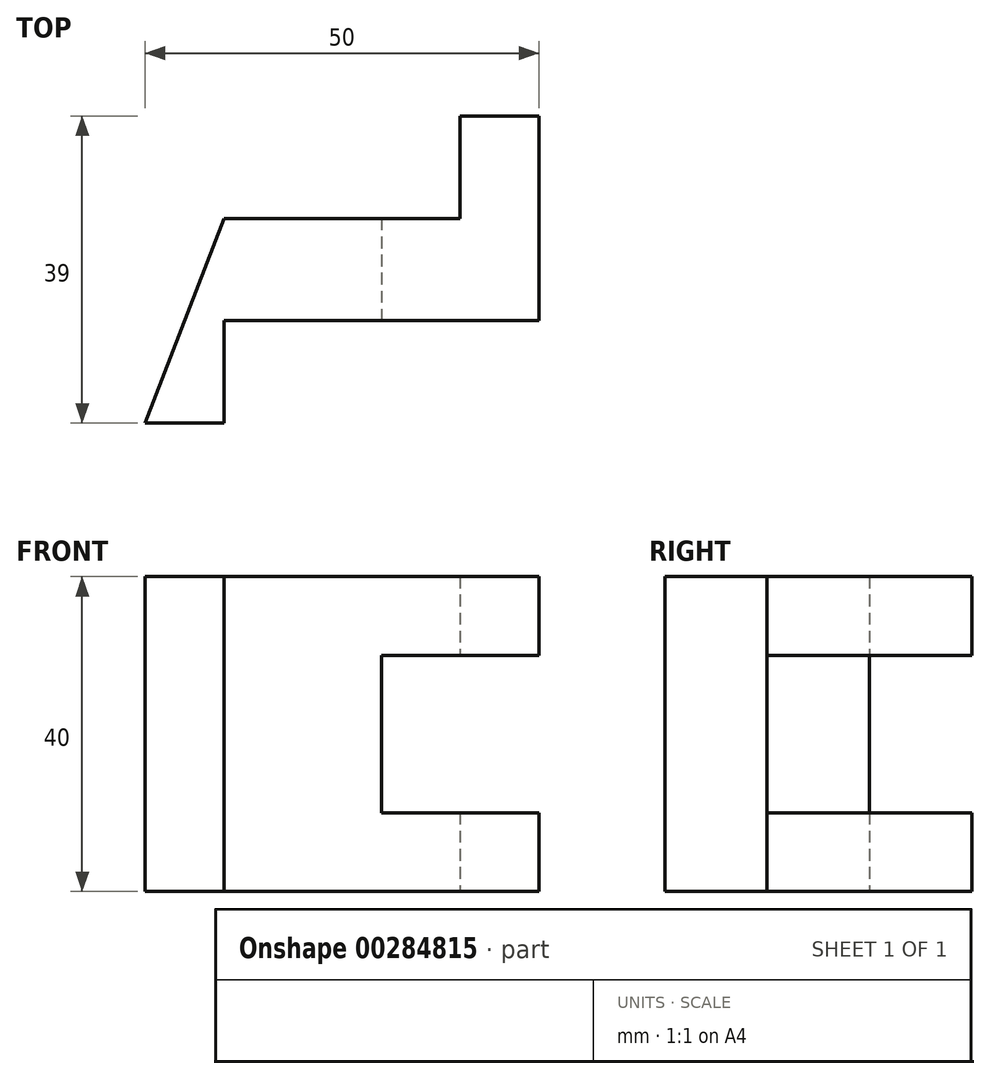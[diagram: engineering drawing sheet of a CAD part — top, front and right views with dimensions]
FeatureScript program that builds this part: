
annotation { "Feature Type Name" : "Feature", "Feature Type Description" : "" }
export const myFeature = defineFeature(function(context is Context, id is Id, definition is map)
    precondition{}
    {
        {
            var Q0;
            Q0=qCreatedBy(makeId("Top.planeOp"),FACE);
            var sketch = newSketch(context, id + "F0", { "sketchPlane" : qUnion([Q0])});
            skLineSegment(sketch, "E0.bottom", {"start": v(0, 0) * mm, "end": v(50, 0) * mm});
            skLineSegment(sketch, "E0.top", {"start": v(0, 39) * mm, "end": v(50, 39) * mm});
            skLineSegment(sketch, "E0.left", {"start": v(0, 0) * mm, "end": v(0, 39) * mm});
            skLineSegment(sketch, "E0.right", {"start": v(50, 0) * mm, "end": v(50, 39) * mm});
            skLineSegment(sketch, "E1", {"start": v(10, 0) * mm, "end": v(10, 13) * mm});
            skLineSegment(sketch, "E2", {"start": v(10, 13) * mm, "end": v(50, 13) * mm});
            skLineSegment(sketch, "E3", {"start": v(40, 39) * mm, "end": v(40, 26) * mm});
            skLineSegment(sketch, "E4", {"start": v(40, 26) * mm, "end": v(0, 26) * mm});
            skSolve(sketch);
        }
        {
            var Q0;
            {var subQ9=sQuery(id+"F0.wireOp",EDGE,"E1");Q0=makeQuery(id+"F0.imprint","IMPRINT",FACE,{"disambiguationData":[TD([[makeQuery(id+"F0.imprint","IMPRINT",EDGE,{"derivedFrom":subQ9}),1.0]])]});}
            extrude(context, id + "F1", {"entities" : qUnion([Q0]), "depth" : 40 * mm, "symmetric" : true});
        }
        {
            var Q0;
            Q0=makeQuery(id+"F1.opExtrude","SWEPT_FACE",FACE,{"disambiguationData":[OSD([sQuery(id+"F0.wireOp",EDGE,"E2")])]});
            var sketch = newSketch(context, id + "F2", { "sketchPlane" : qUnion([Q0])});
            skLineSegment(sketch, "E5.bottom", {"start": v(50, 10) * mm, "end": v(30, 10) * mm});
            skLineSegment(sketch, "E5.top", {"start": v(50, -10) * mm, "end": v(30, -10) * mm});
            skLineSegment(sketch, "E5.left", {"start": v(50, 10) * mm, "end": v(50, -10) * mm});
            skLineSegment(sketch, "E5.right", {"start": v(30, 10) * mm, "end": v(30, -10) * mm});
            skSolve(sketch);
        }
        {
            var Q0;
            Q0=qSketchRegion(id+"F2",true);
            extrude(context, id + "F3", {"entities" : qUnion([Q0]), "operationType" : NewBodyOperationType.REMOVE, "endBound" : BoundingType.THROUGH_ALL, "oppositeDirection" : true, "depth" : 25 * mm});
        }
        {
            var Q0;
            Q0=makeQuery(id+"F1.opExtrude","CAP_FACE",FACE,{"disambiguationData":[OSD([sQuery(id+"F0.wireOp",EDGE,"E0.bottom"),sQuery(id+"F0.wireOp",EDGE,"E0.top"),sQuery(id+"F0.wireOp",EDGE,"E0.left"),sQuery(id+"F0.wireOp",EDGE,"E0.right"),sQuery(id+"F0.wireOp",EDGE,"E1"),sQuery(id+"F0.wireOp",EDGE,"E2"),sQuery(id+"F0.wireOp",EDGE,"E3"),sQuery(id+"F0.wireOp",EDGE,"E4")])],"isStart":false});
            var sketch = newSketch(context, id + "F4", { "sketchPlane" : qUnion([Q0])});
            skLineSegment(sketch, "E6", {"start": v(10, 26) * mm, "end": v(0, 0) * mm});
            skLineSegment(sketch, "E7", {"start": v(0, 0) * mm, "end": v(0, 26) * mm});
            skLineSegment(sketch, "E8", {"start": v(0, 26) * mm, "end": v(10, 26) * mm});
            skSolve(sketch);
        }
        {
            var Q0;
            Q0=makeQuery(id+"F4.imprint","IMPRINT",FACE,{"disambiguationData":[TD([[makeQuery(id+"F4.imprint","IMPRINT",EDGE,{"derivedFrom":sQuery(id+"F4.wireOp",EDGE,"E6")}),-1.0]])]});
            extrude(context, id + "F5", {"entities" : qUnion([Q0]), "operationType" : NewBodyOperationType.REMOVE, "endBound" : BoundingType.THROUGH_ALL, "oppositeDirection" : true, "depth" : 25 * mm});
        }
    });
